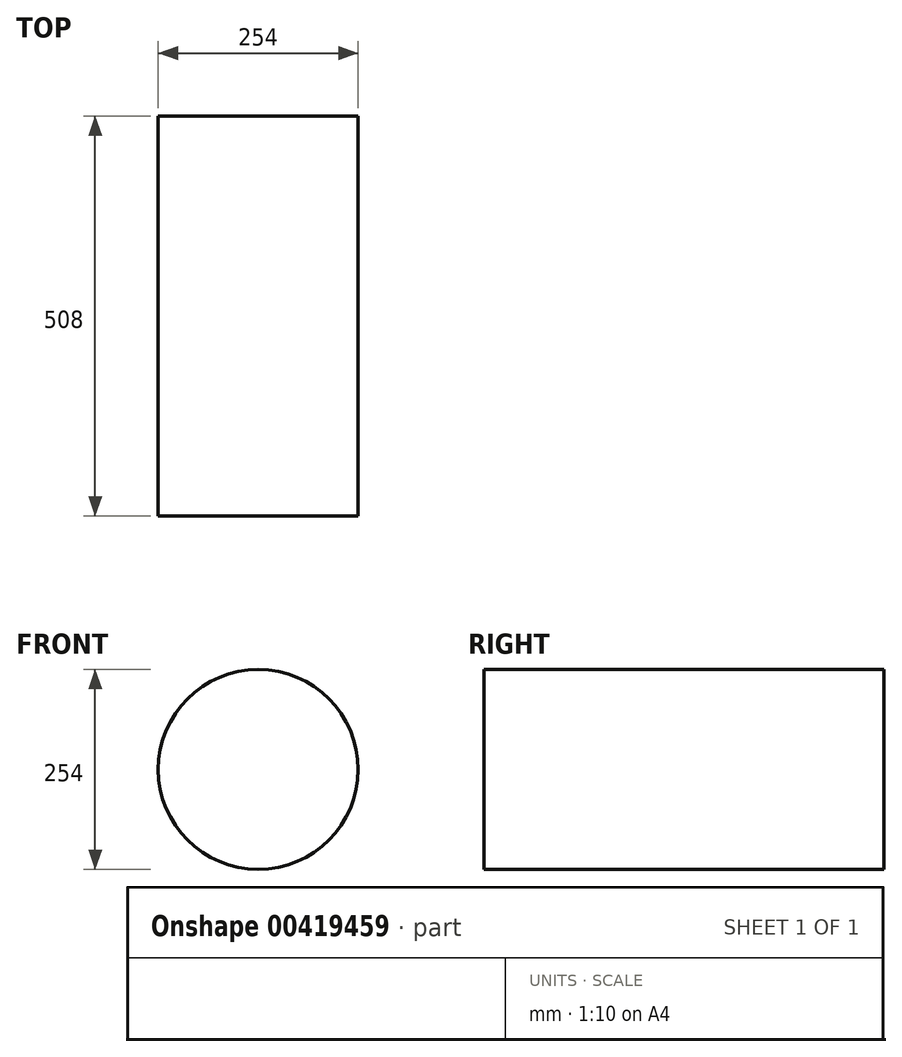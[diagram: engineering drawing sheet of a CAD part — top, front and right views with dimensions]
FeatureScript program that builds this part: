
annotation { "Feature Type Name" : "Feature", "Feature Type Description" : "" }
export const myFeature = defineFeature(function(context is Context, id is Id, definition is map)
    precondition{}
    {
        {
            var Q0;
            Q0=qCreatedBy(makeId("Front.planeOp"),FACE);
            var sketch = newSketch(context, id + "F0", { "sketchPlane" : qUnion([Q0])});
            skCircle(sketch, "E0", {"center": v(0, 0) * mm, "radius": 127 * mm});
            skSolve(sketch);
        }
        {
            var Q0;
            Q0=makeQuery(id+"F0.imprint","IMPRINT",FACE,{"disambiguationData":[TD([[makeQuery(id+"F0.imprint","IMPRINT",EDGE,{"derivedFrom":sQuery(id+"F0.wireOp",EDGE,"E0")}),1.0]])]});
            extrude(context, id + "F1", {"entities" : qUnion([Q0]), "depth" : 254 * mm});
        }
        {
            var Q0;
            Q0=makeQuery(id+"F1.opExtrude","CAP_FACE",FACE,{"disambiguationData":[OSD([sQuery(id+"F0.wireOp",EDGE,"E0")])],"isStart":true});
            var sketch = newSketch(context, id + "F2", { "sketchPlane" : qUnion([Q0])});
            skCircle(sketch, "E1", {"center": v(0, 0) * mm, "radius": 127 * mm});
            skSolve(sketch);
        }
        {
            var Q0;
            Q0=makeQuery(id+"F1.opExtrude","CAP_FACE",FACE,{"disambiguationData":[OSD([sQuery(id+"F0.wireOp",EDGE,"E0")])],"isStart":true});
            var Q1;
            Q1=makeQuery(id+"F2.imprint","IMPRINT",FACE,{"disambiguationData":[TD([[makeQuery(id+"F2.imprint","IMPRINT",EDGE,{"derivedFrom":sQuery(id+"F2.wireOp",EDGE,"E1")}),-1.0]])]});
            extrude(context, id + "F3", {"entities" : qUnion([Q0, Q1]), "operationType" : NewBodyOperationType.ADD, "depth" : 254 * mm});
        }
    });
